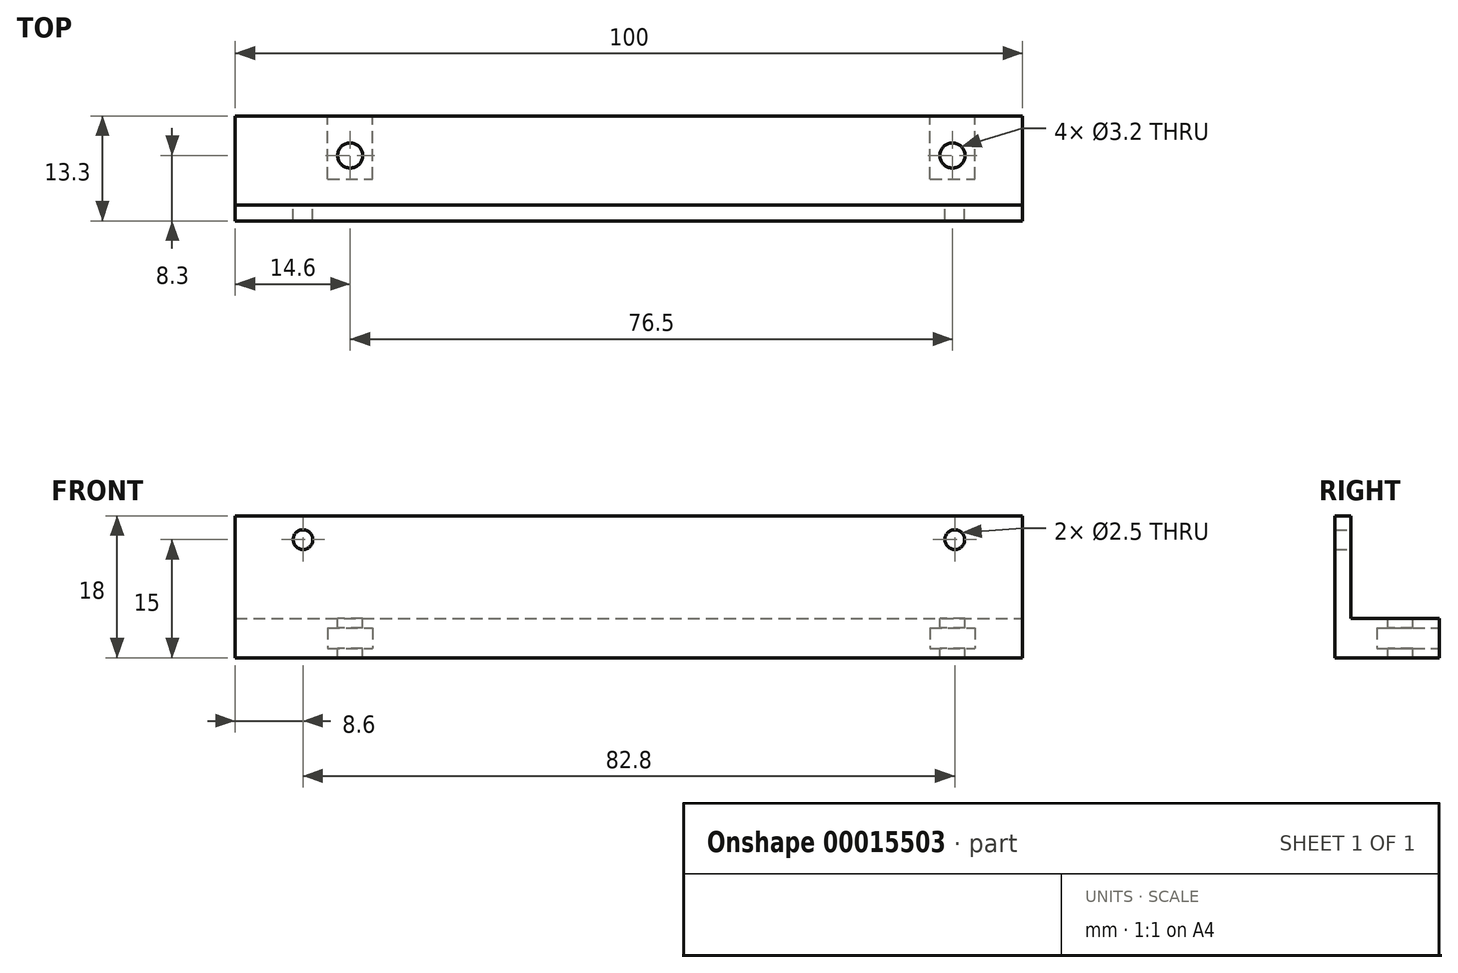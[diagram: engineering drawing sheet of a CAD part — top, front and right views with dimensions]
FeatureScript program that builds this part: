
annotation { "Feature Type Name" : "Feature", "Feature Type Description" : "" }
export const myFeature = defineFeature(function(context is Context, id is Id, definition is map)
    precondition{}
    {
        {
            var Q0;
            Q0=qCreatedBy(makeId("Top.planeOp"),FACE);
            var sketch = newSketch(context, id + "F0", { "sketchPlane" : qUnion([Q0])});
            skLineSegment(sketch, "E0.rect.bottom", {"start": v(50, 0) * mm, "end": v(-50, 0) * mm});
            skLineSegment(sketch, "E0.rect.top", {"start": v(50, -2) * mm, "end": v(-50, -2) * mm});
            skLineSegment(sketch, "E0.rect.left", {"start": v(50, 0) * mm, "end": v(50, -2) * mm});
            skLineSegment(sketch, "E0.rect.right", {"start": v(-50, 0) * mm, "end": v(-50, -2) * mm});
            skPoint(sketch, "E0.rect.middle", {"position": v(0, 0) * mm});
            skSolve(sketch);
        }
        {
            var Q0;
            Q0=qSketchRegion(id+"F0",true);
            extrude(context, id + "F1", {"entities" : qUnion([Q0]), "depth" : 13 * mm});
        }
        {
            var Q0;
            Q0=qCreatedBy(makeId("Front.planeOp"),FACE);
            var sketch = newSketch(context, id + "F2", { "sketchPlane" : qUnion([Q0])});
            skPoint(sketch, "E1", {"position": v(-41.4, 10) * mm});
            skPoint(sketch, "E2", {"position": v(41.4, 10) * mm});
            skLineSegment(sketch, "E3", {"start": v(-41.4, 10) * mm, "end": v(41.4, 10) * mm, "construction": true});
            skLineSegment(sketch, "E4", {"start": v(0, 0) * mm, "end": v(0, 10) * mm, "construction": true});
            skSolve(sketch);
        }
        {
            var Q0;
            Q0=sQuery(id+"F2.wireOp",VERTEX,"E2");
            var Q1;
            Q1=sQuery(id+"F2.wireOp",VERTEX,"E1");
            var Q2;
            Q2=makeQuery(id+"F1.opExtrude","SWEPT_BODY",BODY,{"disambiguationData":[OSD([sQuery(id+"F0.wireOp",EDGE,"E0.rect.bottom"),sQuery(id+"F0.wireOp",EDGE,"E0.rect.top"),sQuery(id+"F0.wireOp",EDGE,"E0.rect.left"),sQuery(id+"F0.wireOp",EDGE,"E0.rect.right")])]});
            hole(context, id + "F3", {"style" : HoleStyle.SIMPLE, "holeDiameter" : 2.5 * mm, "endStyle" : HoleEndStyle.THROUGH, "oppositeDirection" : true, "locations" : qUnion([Q0, Q1]), "scope" : qUnion([Q2])});
        }
        {
            var Q0;
            Q0=qCreatedBy(makeId("Top.planeOp"),FACE);
            var sketch = newSketch(context, id + "F4", { "sketchPlane" : qUnion([Q0])});
            skLineSegment(sketch, "E5.bottom", {"start": v(-50, -2) * mm, "end": v(50, -2) * mm});
            skLineSegment(sketch, "E5.top", {"start": v(-50, 11.3) * mm, "end": v(50, 11.3) * mm});
            skLineSegment(sketch, "E5.left", {"start": v(-50, -2) * mm, "end": v(-50, 11.3) * mm});
            skLineSegment(sketch, "E5.right", {"start": v(50, -2) * mm, "end": v(50, 11.3) * mm});
            skSolve(sketch);
        }
        {
            var Q0;
            Q0=qSketchRegion(id+"F4",true);
            extrude(context, id + "F5", {"entities" : qUnion([Q0]), "operationType" : NewBodyOperationType.ADD, "oppositeDirection" : true, "depth" : 5 * mm});
        }
        {
            var Q0;
            Q0=qCreatedBy(makeId("Top.planeOp"),FACE);
            var sketch = newSketch(context, id + "F6", { "sketchPlane" : qUnion([Q0])});
            skLineSegment(sketch, "E6", {"start": v(41.1, 6.3) * mm, "end": v(-35.4, 6.3) * mm, "construction": true});
            skPoint(sketch, "E7", {"position": v(-35.4, 6.3) * mm});
            skPoint(sketch, "E8", {"position": v(41.1, 6.3) * mm});
            skSolve(sketch);
        }
        {
            var Q0;
            Q0=sQuery(id+"F6.wireOp",VERTEX,"E7");
            var Q1;
            Q1=sQuery(id+"F6.wireOp",VERTEX,"E8");
            var Q2;
            Q2=makeQuery(id+"F1.opExtrude","SWEPT_BODY",BODY,{"disambiguationData":[OSD([sQuery(id+"F0.wireOp",EDGE,"E0.rect.bottom"),sQuery(id+"F0.wireOp",EDGE,"E0.rect.top"),sQuery(id+"F0.wireOp",EDGE,"E0.rect.left"),sQuery(id+"F0.wireOp",EDGE,"E0.rect.right")])]});
            hole(context, id + "F7", {"style" : HoleStyle.SIMPLE, "holeDiameter" : 3.2 * mm, "endStyle" : HoleEndStyle.THROUGH, "locations" : qUnion([Q0, Q1]), "scope" : qUnion([Q2])});
        }
        {
            var Q0;
            Q0=makeQuery(id+"F5.opExtrude","SWEPT_FACE",FACE,{"disambiguationData":[OSD([sQuery(id+"F4.wireOp",EDGE,"E5.top")])]});
            var sketch = newSketch(context, id + "F8", { "sketchPlane" : qUnion([Q0])});
            skLineSegment(sketch, "E9", {"start": v(-41.1, 0) * mm, "end": v(-41.1, -2.5) * mm, "construction": true});
            skLineSegment(sketch, "E10", {"start": v(35.4, 0) * mm, "end": v(35.4, -2.5) * mm, "construction": true});
            skLineSegment(sketch, "E11.rect.bottom", {"start": v(-38.25, -1.2) * mm, "end": v(-43.95, -1.2) * mm});
            skLineSegment(sketch, "E11.rect.top", {"start": v(-38.25, -3.8) * mm, "end": v(-43.95, -3.8) * mm});
            skLineSegment(sketch, "E11.rect.left", {"start": v(-38.25, -1.2) * mm, "end": v(-38.25, -3.8) * mm});
            skLineSegment(sketch, "E11.rect.right", {"start": v(-43.95, -1.2) * mm, "end": v(-43.95, -3.8) * mm});
            skPoint(sketch, "E11.rect.middle", {"position": v(-41.1, -2.5) * mm});
            skLineSegment(sketch, "E12.rect.bottom", {"start": v(38.25, -3.8) * mm, "end": v(32.55, -3.8) * mm});
            skLineSegment(sketch, "E12.rect.top", {"start": v(38.25, -1.2) * mm, "end": v(32.55, -1.2) * mm});
            skLineSegment(sketch, "E12.rect.left", {"start": v(32.55, -1.2) * mm, "end": v(32.55, -3.8) * mm});
            skLineSegment(sketch, "E12.rect.right", {"start": v(38.25, -1.2) * mm, "end": v(38.25, -3.8) * mm});
            skPoint(sketch, "E12.rect.middle", {"position": v(35.4, -2.5) * mm});
            skSolve(sketch);
        }
        {
            var Q0;
            Q0 = qSketchRegion(id + "F8", true);
            extrude(context, id + "F9", {"entities" : qUnion([Q0]), "operationType" : NewBodyOperationType.REMOVE, "oppositeDirection" : true, "depth" : (5 + 3) * mm});
        }
    });
